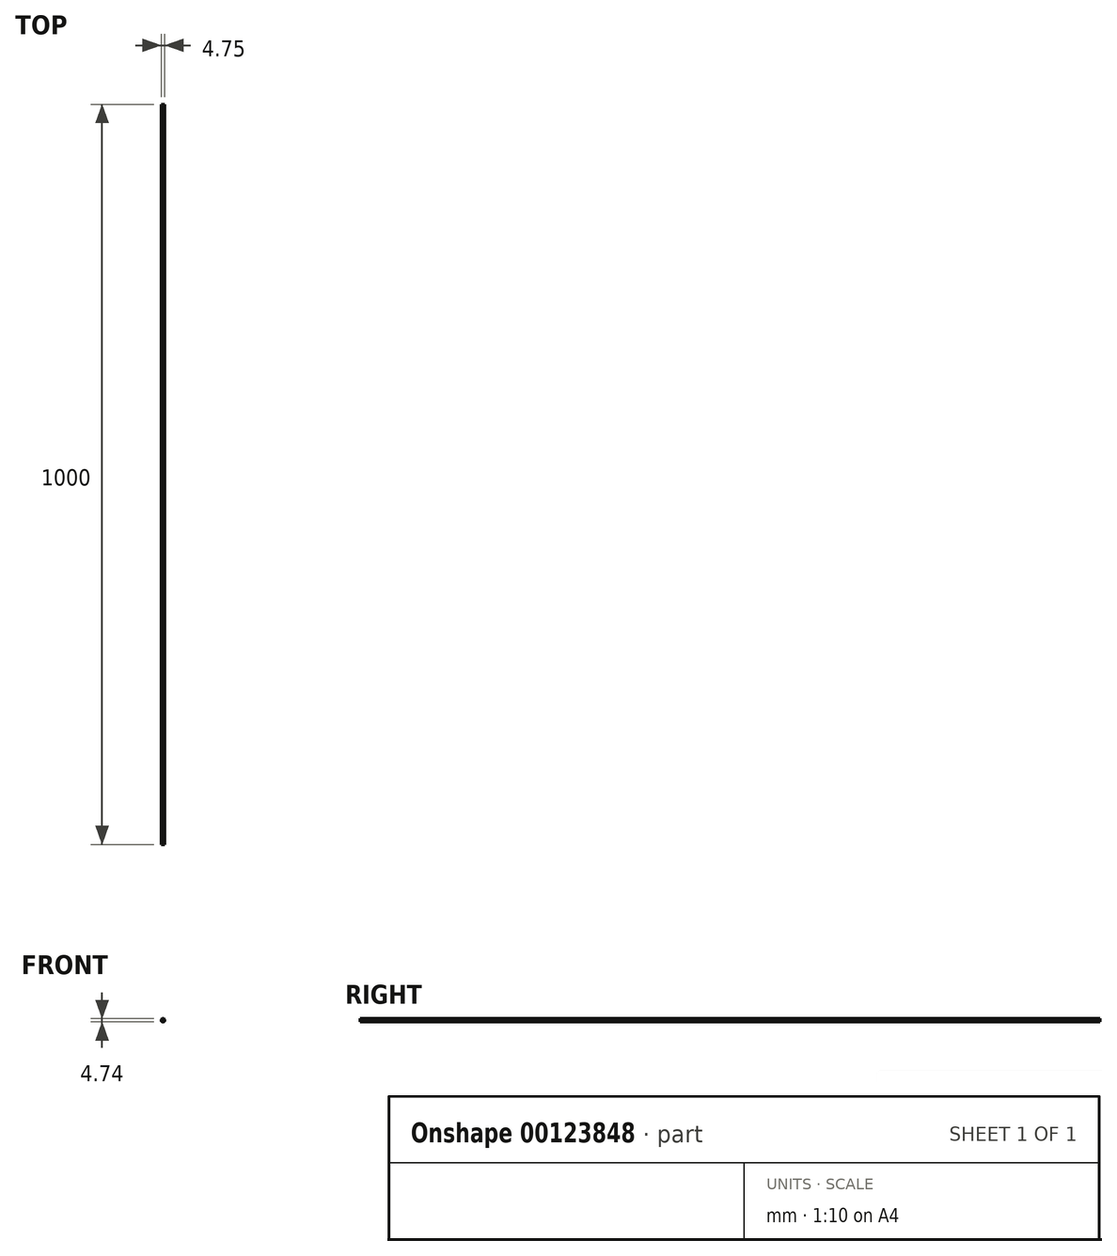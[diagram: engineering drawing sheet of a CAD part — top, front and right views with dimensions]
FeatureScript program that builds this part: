
annotation { "Feature Type Name" : "Feature", "Feature Type Description" : "" }
export const myFeature = defineFeature(function(context is Context, id is Id, definition is map)
    precondition{}
    {
        {
            var Q0;
            Q0=qCreatedBy(makeId("Front.planeOp"),FACE);
            var sketch = newSketch(context, id + "F0", { "sketchPlane" : qUnion([Q0])});
            skCircle(sketch, "E0", {"center": v(-37.83, 34.51) * mm, "radius": 2.37 * mm});
            skSolve(sketch);
        }
        {
            var Q0;
            Q0=makeQuery(id+"F0.imprint","IMPRINT",FACE,{"disambiguationData":[TD([[makeQuery(id+"F0.imprint","IMPRINT",EDGE,{"derivedFrom":sQuery(id+"F0.wireOp",EDGE,"E0")}),1.0]])]});
            extrude(context, id + "F1", {"entities" : qUnion([Q0]), "depth" : 1000 * mm, "offsetDistance" : 25 * mm});
        }
    });
